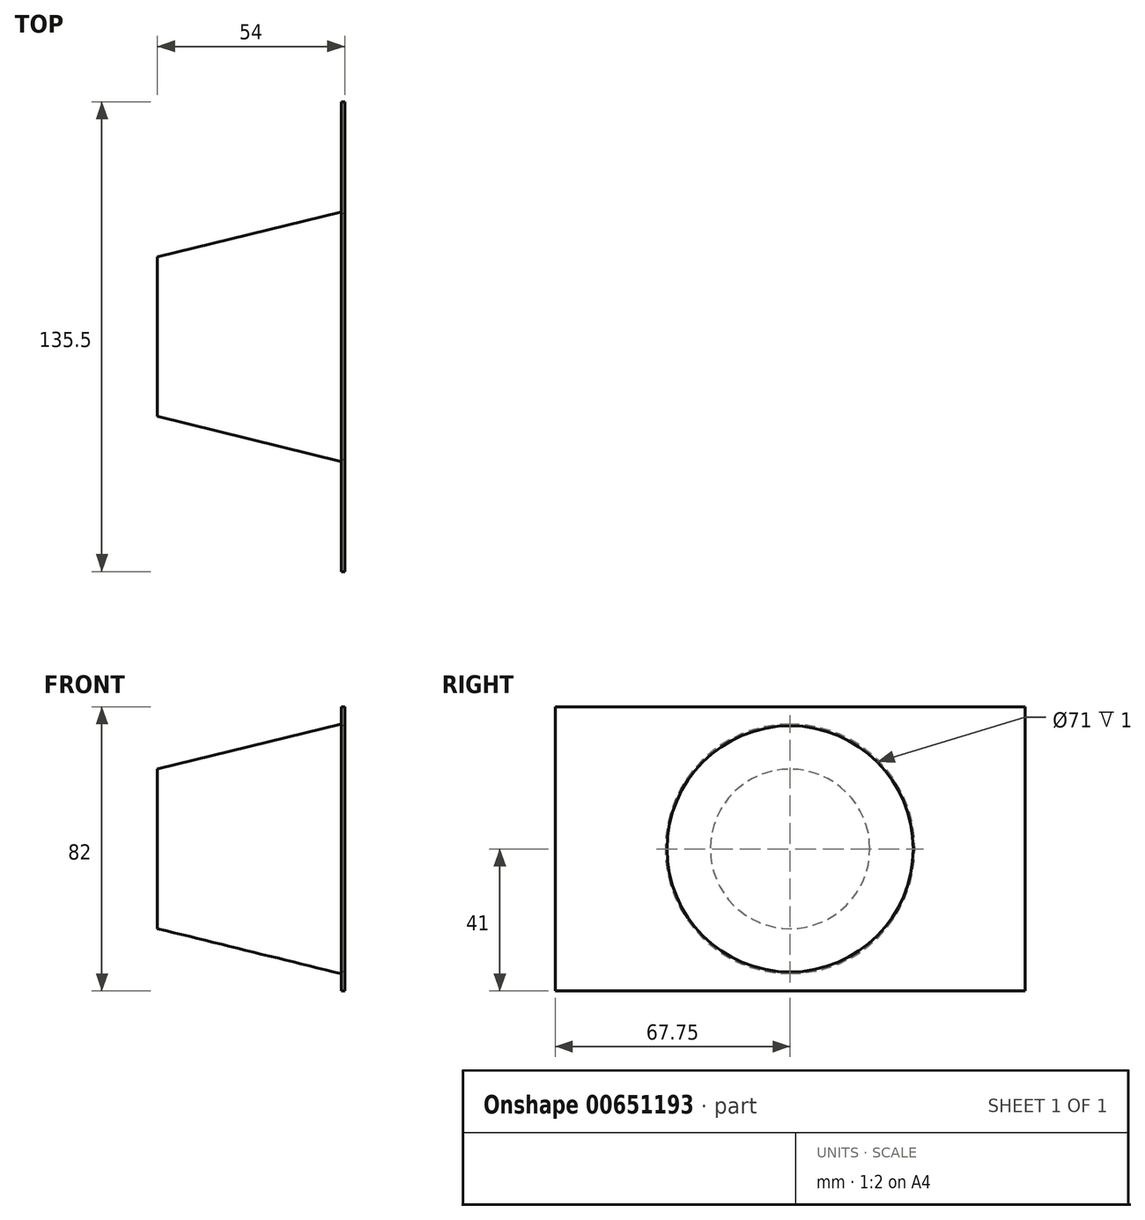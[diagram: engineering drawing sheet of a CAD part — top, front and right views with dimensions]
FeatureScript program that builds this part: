
annotation { "Feature Type Name" : "Feature", "Feature Type Description" : "" }
export const myFeature = defineFeature(function(context is Context, id is Id, definition is map)
    precondition{}
    {
        {
            var Q0;
            Q0=qCreatedBy(makeId("Right.planeOp"),FACE);
            var sketch = newSketch(context, id + "F0", { "sketchPlane" : qUnion([Q0])});
            skLineSegment(sketch, "E0.bottom", {"start": v(-67.75, 41) * mm, "end": v(67.75, 41) * mm});
            skLineSegment(sketch, "E0.top", {"start": v(-67.75, -41) * mm, "end": v(67.75, -41) * mm});
            skLineSegment(sketch, "E0.left", {"start": v(-67.75, 41) * mm, "end": v(-67.75, -41) * mm});
            skLineSegment(sketch, "E0.right", {"start": v(67.75, 41) * mm, "end": v(67.75, -41) * mm});
            skPoint(sketch, "E0.middle", {"position": v(0, 0) * mm});
            skCircle(sketch, "E1", {"center": v(0, 0) * mm, "radius": 35.5 * mm});
            skSolve(sketch);
        }
        {
            var Q0;
            Q0 = qSketchRegion(id + "F0", true);
            extrude(context, id + "F1", {"entities" : qUnion([Q0]), "depth" : 1 * mm, "offsetDistance" : 25 * mm});
        }
        {
            var Q0;
            Q0=makeQuery(id+"F1.opExtrude","CAP_FACE",FACE,{"disambiguationData":[OSD([sQuery(id+"F0.wireOp",EDGE,"E0.bottom"),sQuery(id+"F0.wireOp",EDGE,"E0.top"),sQuery(id+"F0.wireOp",EDGE,"E0.left"),sQuery(id+"F0.wireOp",EDGE,"E0.right")])],"isStart":true});
            var sketch = newSketch(context, id + "F2", { "sketchPlane" : qUnion([Q0])});
            skCircle(sketch, "E2", {"center": v(0, 0) * mm, "radius": 36 * mm});
            skSolve(sketch);
        }
        {
            var Q0;
            Q0=qCreatedBy(makeId("Right.planeOp"),FACE);
            cPlane(context, id + "F3", {"entities" : qUnion([Q0]), "cplaneType" : CPlaneType.OFFSET, "offset" : 53 * mm, "oppositeDirection" : true, "width" : 150 * mm, "height" : 150 * mm});
        }
        {
            var Q0;
            Q0=qCreatedBy(id+"F3.planeOp",FACE);
            var sketch = newSketch(context, id + "F4", { "sketchPlane" : qUnion([Q0])});
            skCircle(sketch, "E3", {"center": v(0, 0) * mm, "radius": 23 * mm});
            skSolve(sketch);
        }
        {
            var Q1;
            Q1 = qSketchRegion(id + "F2", true);
            var Q2;
            Q2 = qSketchRegion(id + "F4", true);
            loft(context, id + "F5", {"operationType" : NewBodyOperationType.ADD, "sheetProfilesArray" : [{ "sheetProfileEntities" : qUnion([Q1]) }, { "sheetProfileEntities" : qUnion([Q2]) }]});
        }
    });
